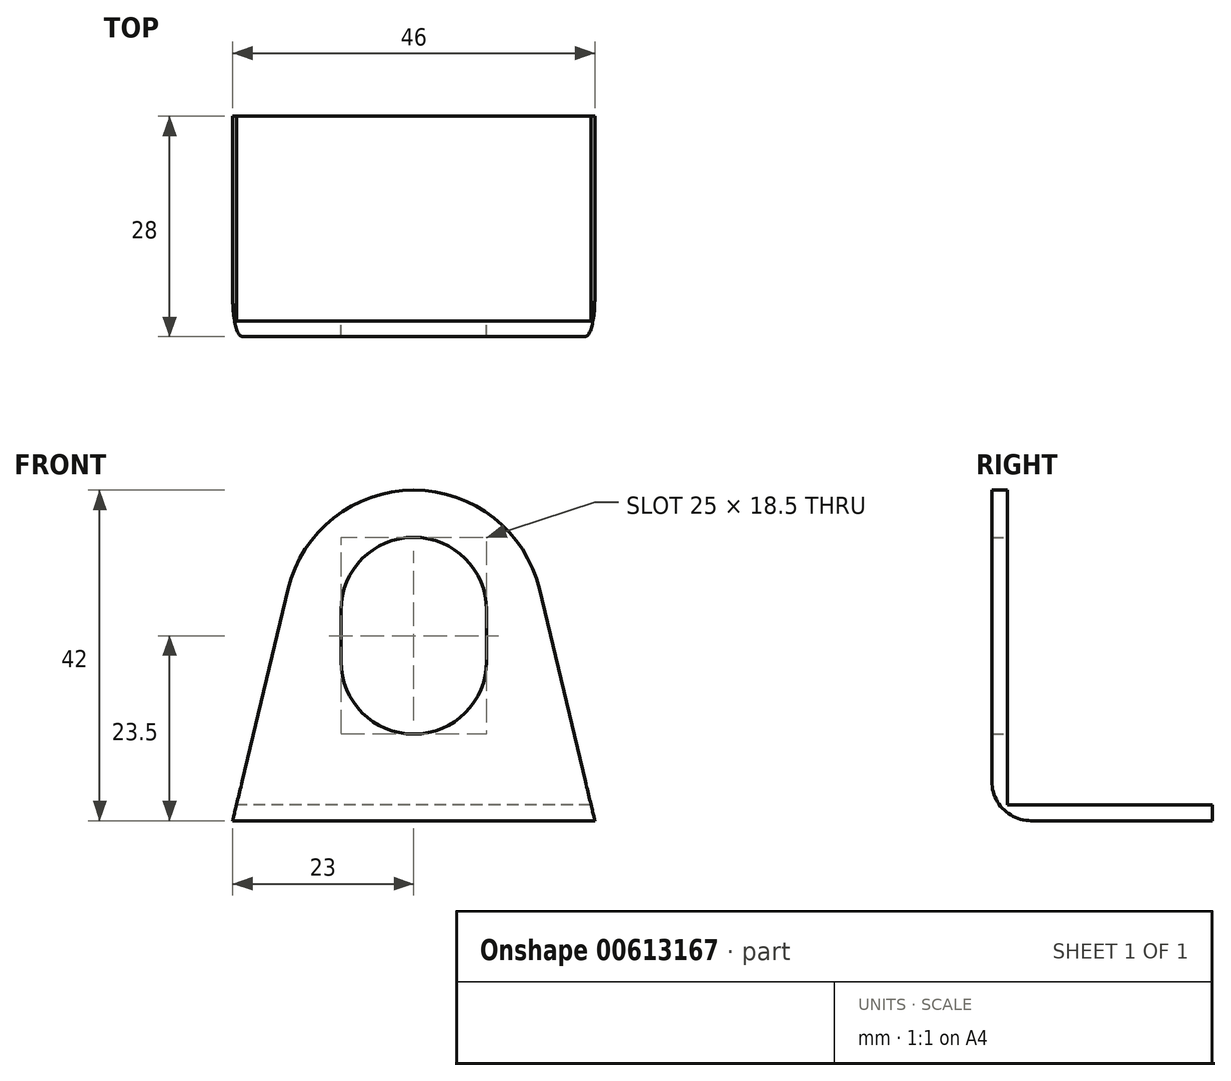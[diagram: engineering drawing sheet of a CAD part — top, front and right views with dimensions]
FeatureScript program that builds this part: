
annotation { "Feature Type Name" : "Feature", "Feature Type Description" : "" }
export const myFeature = defineFeature(function(context is Context, id is Id, definition is map)
    precondition{}
    {
        {
            var Q0;
            Q0=qCreatedBy(makeId("Front.planeOp"),FACE);
            var sketch = newSketch(context, id + "F0", { "sketchPlane" : qUnion([Q0])});
            skLineSegment(sketch, "E0", {"start": v(-23, 0) * mm, "end": v(23, 0) * mm});
            skLineSegment(sketch, "E1", {"start": v(23, 0) * mm, "end": v(15.96, 29.41) * mm});
            skLineSegment(sketch, "E2", {"start": v(-23, 0) * mm, "end": v(-15.96, 29.41) * mm});
            skArc(sketch, "E3", {"start": v(15.96, 29.41) * mm, "mid": v(0, 42) * mm, "end": v(-15.96, 29.41) * mm});
            skLineSegment(sketch, "E4", {"start": v(-9.25, 26.75) * mm, "end": v(-9.25, 20.25) * mm});
            skLineSegment(sketch, "E5", {"start": v(9.25, 26.75) * mm, "end": v(9.25, 20.25) * mm});
            skArc(sketch, "E6", {"start": v(-9.25, 20.25) * mm, "mid": v(0, 11) * mm, "end": v(9.25, 20.25) * mm});
            skArc(sketch, "E7", {"start": v(9.25, 26.75) * mm, "mid": v(0, 36) * mm, "end": v(-9.25, 26.75) * mm});
            skPoint(sketch, "E8", {"position": v(0, 0) * mm});
            skPoint(sketch, "E9", {"position": v(0, 42) * mm});
            skSolve(sketch);
        }
        {
            var Q0;
            Q0=qSketchRegion(id+"F0",true);
            extrude(context, id + "F1", {"entities" : qUnion([Q0]), "depth" : 2 * mm, "offsetDistance" : 25 * mm});
        }
        {
            var Q0;
            Q0=makeQuery(id+"F1.opExtrude","CAP_FACE",FACE,{"disambiguationData":[OSD([sQuery(id+"F0.wireOp",EDGE,"E0"),sQuery(id+"F0.wireOp",EDGE,"E1"),sQuery(id+"F0.wireOp",EDGE,"E2"),sQuery(id+"F0.wireOp",EDGE,"E3"),sQuery(id+"F0.wireOp",EDGE,"E4"),sQuery(id+"F0.wireOp",EDGE,"E5"),sQuery(id+"F0.wireOp",EDGE,"E6"),sQuery(id+"F0.wireOp",EDGE,"E7")])],"isStart":true});
            var sketch = newSketch(context, id + "F2", { "sketchPlane" : qUnion([Q0])});
            skLineSegment(sketch, "E10", {"start": v(-22.52, 2) * mm, "end": v(22.52, 2) * mm});
            skSolve(sketch);
        }
        {
            var Q0;
            {var subQ0=sQuery(id+"F2.wireOp",EDGE,"E10");Q0=makeQuery(id+"F2.imprint","IMPRINT",FACE,{"disambiguationData":[TD([[makeQuery(id+"F2.imprint","IMPRINT",EDGE,{"derivedFrom":subQ0}),-1.0]])]});}
            extrude(context, id + "F3", {"entities" : qUnion([Q0]), "operationType" : NewBodyOperationType.ADD, "depth" : 26 * mm, "offsetDistance" : 25 * mm});
        }
        {
            var Q0;
            Q0=makeQuery(id+"F1.opExtrude","CAP_EDGE",EDGE,{"disambiguationData":[OSD([sQuery(id+"F0.wireOp",EDGE,"E0")])],"isStart":false});
            var Q1;
            Q1=makeQuery(id+"F3.opExtrude","CAP_EDGE",EDGE,{"disambiguationData":[OSD([sQuery(id+"F2.wireOp",EDGE,"E10")])],"isStart":true});
            fillet(context, id + "F4", {"entities" : qUnion([Q0, Q1]), "radius" : 5 * mm, "tangentPropagation" : true, "allowEdgeOverflow" : false});
        }
    });
